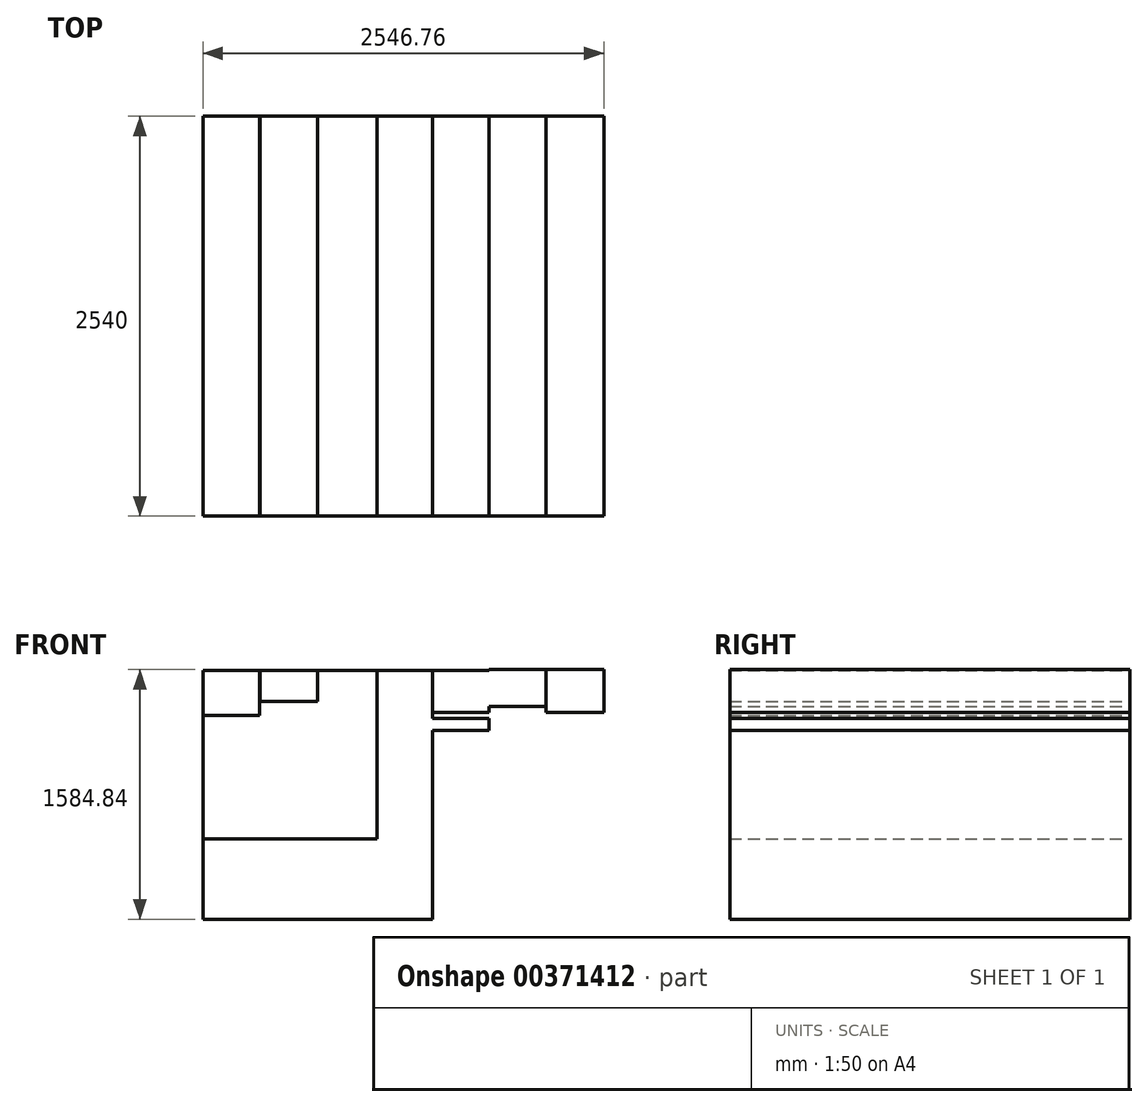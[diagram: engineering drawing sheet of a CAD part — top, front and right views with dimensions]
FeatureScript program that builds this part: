
annotation { "Feature Type Name" : "Feature", "Feature Type Description" : "" }
export const myFeature = defineFeature(function(context is Context, id is Id, definition is map)
    precondition{}
    {
        {
            var Q0;
            Q0=qCreatedBy(makeId("Front.planeOp"),FACE);
            var sketch = newSketch(context, id + "F0", { "sketchPlane" : qUnion([Q0])});
            skLineSegment(sketch, "E0", {"start": v(-1277.32, 1268.25) * mm, "end": v(-1277.32, -1271.75) * mm});
            skLineSegment(sketch, "E1", {"start": v(-1277.32, -1271.75) * mm, "end": v(1269.44, -1271.75) * mm});
            skLineSegment(sketch, "E2", {"start": v(1269.44, -1271.75) * mm, "end": v(1269.44, 1273.33) * mm});
            skLineSegment(sketch, "E3", {"start": v(1269.44, 1273.33) * mm, "end": v(-1277.32, 1268.25) * mm});
            skLineSegment(sketch, "E4", {"start": v(-1277.32, 1268.25) * mm, "end": v(-914.1, 1268.98) * mm});
            skLineSegment(sketch, "E5", {"start": v(-914.1, 1268.98) * mm, "end": v(-550.88, 1269.7) * mm});
            skLineSegment(sketch, "E6", {"start": v(-550.88, 1269.7) * mm, "end": v(-187.66, 1270.42) * mm});
            skLineSegment(sketch, "E7", {"start": v(-187.66, 1270.42) * mm, "end": v(175.56, 1271.15) * mm});
            skLineSegment(sketch, "E8", {"start": v(175.56, 1271.15) * mm, "end": v(538.78, 1271.87) * mm});
            skLineSegment(sketch, "E9", {"start": v(538.78, 1271.87) * mm, "end": v(902, 1272.6) * mm});
            skLineSegment(sketch, "E10", {"start": v(902, 1272.6) * mm, "end": v(1269.44, 1273.33) * mm});
            skLineSegment(sketch, "E11.bottom", {"start": v(-1277.32, 1268.25) * mm, "end": v(-917.92, 1268.25) * mm});
            skLineSegment(sketch, "E11.top", {"start": v(-1277.32, 980.21) * mm, "end": v(-917.92, 980.21) * mm});
            skLineSegment(sketch, "E11.left", {"start": v(-1277.32, 1268.25) * mm, "end": v(-1277.32, 980.21) * mm});
            skLineSegment(sketch, "E11.right", {"start": v(-917.92, 1268.25) * mm, "end": v(-917.92, 980.21) * mm});
            skLineSegment(sketch, "E12.bottom", {"start": v(-914.1, 1268.98) * mm, "end": v(-550.13, 1268.98) * mm});
            skLineSegment(sketch, "E12.top", {"start": v(-914.1, 1071.1) * mm, "end": v(-550.13, 1071.1) * mm});
            skLineSegment(sketch, "E12.left", {"start": v(-914.1, 1268.98) * mm, "end": v(-914.1, 1071.1) * mm});
            skLineSegment(sketch, "E12.right", {"start": v(-550.13, 1268.98) * mm, "end": v(-550.13, 1071.1) * mm});
            skLineSegment(sketch, "E13.bottom", {"start": v(-1277.32, 1268.25) * mm, "end": v(-172.42, 1268.25) * mm});
            skLineSegment(sketch, "E13.top", {"start": v(-1277.32, 195.83) * mm, "end": v(-172.42, 195.83) * mm});
            skLineSegment(sketch, "E13.left", {"start": v(-1277.32, 1268.25) * mm, "end": v(-1277.32, 195.83) * mm});
            skLineSegment(sketch, "E13.right", {"start": v(-172.42, 1268.25) * mm, "end": v(-172.42, 195.83) * mm});
            skLineSegment(sketch, "E14.bottom", {"start": v(-1277.32, 1268.25) * mm, "end": v(180.77, 1268.25) * mm});
            skLineSegment(sketch, "E14.top", {"start": v(-1277.32, -312.97) * mm, "end": v(180.77, -312.97) * mm});
            skLineSegment(sketch, "E14.left", {"start": v(-1277.32, 1268.25) * mm, "end": v(-1277.32, -312.97) * mm});
            skLineSegment(sketch, "E14.right", {"start": v(180.77, 1268.25) * mm, "end": v(180.77, -312.97) * mm});
            skLineSegment(sketch, "E15.bottom", {"start": v(180.77, 1268.25) * mm, "end": v(538.78, 1268.25) * mm});
            skLineSegment(sketch, "E15.top", {"start": v(180.77, 1000.53) * mm, "end": v(538.78, 1000.53) * mm});
            skLineSegment(sketch, "E15.left", {"start": v(180.77, 1268.25) * mm, "end": v(180.77, 1000.53) * mm});
            skLineSegment(sketch, "E15.right", {"start": v(538.78, 1268.25) * mm, "end": v(538.78, 1000.53) * mm});
            skLineSegment(sketch, "E16.bottom", {"start": v(538.78, 1271.87) * mm, "end": v(902, 1271.87) * mm});
            skLineSegment(sketch, "E16.top", {"start": v(538.78, 1038.28) * mm, "end": v(902, 1038.28) * mm});
            skLineSegment(sketch, "E16.left", {"start": v(538.78, 1271.87) * mm, "end": v(538.78, 1038.28) * mm});
            skLineSegment(sketch, "E16.right", {"start": v(902, 1271.87) * mm, "end": v(902, 1038.28) * mm});
            skLineSegment(sketch, "E17.bottom", {"start": v(902, 1271.87) * mm, "end": v(1269.44, 1271.87) * mm});
            skLineSegment(sketch, "E17.top", {"start": v(902, 1000.53) * mm, "end": v(1269.44, 1000.53) * mm});
            skLineSegment(sketch, "E17.left", {"start": v(902, 1271.87) * mm, "end": v(902, 1000.53) * mm});
            skLineSegment(sketch, "E17.right", {"start": v(1269.44, 1271.87) * mm, "end": v(1269.44, 1000.53) * mm});
            skLineSegment(sketch, "E18", {"start": v(-1277.32, 1268.25) * mm, "end": v(-1277.32, 963.45) * mm});
            skLineSegment(sketch, "E19", {"start": v(-1277.32, 963.45) * mm, "end": v(-1277.32, 1268.25) * mm});
            skLineSegment(sketch, "E20", {"start": v(-1277.32, 887.25) * mm, "end": v(-1277.32, 1268.25) * mm});
            skLineSegment(sketch, "E21.bottom", {"start": v(538.78, 963.45) * mm, "end": v(180.77, 963.45) * mm});
            skLineSegment(sketch, "E21.top", {"start": v(538.78, 887.25) * mm, "end": v(180.77, 887.25) * mm});
            skLineSegment(sketch, "E21.left", {"start": v(538.78, 963.45) * mm, "end": v(538.78, 887.25) * mm});
            skLineSegment(sketch, "E21.right", {"start": v(180.77, 963.45) * mm, "end": v(180.77, 887.25) * mm});
            skSolve(sketch);
        }
        {
            var Q0;
            {var subQ0=sQuery(id+"F0.wireOp",EDGE,"E11.top");Q0=makeQuery(id+"F0.imprint","IMPRINT",FACE,{"disambiguationData":[TD([[makeQuery(id+"F0.imprint","IMPRINT",EDGE,{"derivedFrom":subQ0}),1.0]])]});}
            var Q1;
            {var subQ3=sQuery(id+"F0.wireOp",EDGE,"E16.bottom");Q1=makeQuery(id+"F0.imprint","IMPRINT",FACE,{"disambiguationData":[TD([[makeQuery(id+"F0.imprint","IMPRINT",EDGE,{"derivedFrom":subQ3}),-1.0]])]});}
            extrude(context, id + "F1", {"entities" : qUnion([Q0, Q1]), "depth" : 2540 * mm});
        }
        {
            var Q0;
            {var subQ0=sQuery(id+"F0.wireOp",EDGE,"E12.top");Q0=makeQuery(id+"F0.imprint","IMPRINT",FACE,{"disambiguationData":[TD([[makeQuery(id+"F0.imprint","IMPRINT",EDGE,{"derivedFrom":subQ0}),1.0]])]});}
            var Q1;
            {var subQ1=sQuery(id+"F0.wireOp",EDGE,"E15.bottom");Q1=makeQuery(id+"F0.imprint","IMPRINT",FACE,{"disambiguationData":[TD([[makeQuery(id+"F0.imprint","IMPRINT",EDGE,{"derivedFrom":subQ1}),-1.0]])]});}
            extrude(context, id + "F2", {"entities" : qUnion([Q0, Q1]), "operationType" : NewBodyOperationType.ADD, "depth" : 2540 * mm});
        }
        {
            var Q0;
            {var subQ9=sQuery(id+"F0.wireOp",EDGE,"E11.top");Q0=makeQuery(id+"F0.imprint","IMPRINT",FACE,{"disambiguationData":[TD([[makeQuery(id+"F0.imprint","IMPRINT",EDGE,{"derivedFrom":subQ9}),-1.0]])]});}
            var Q1;
            {var subQ4=sQuery(id+"F0.wireOp",EDGE,"E13.top");Q1=makeQuery(id+"F0.imprint","IMPRINT",FACE,{"disambiguationData":[TD([[makeQuery(id+"F0.imprint","IMPRINT",EDGE,{"derivedFrom":subQ4}),-1.0]])]});}
            var Q2;
            Q2=makeQuery(id+"F0.imprint","IMPRINT",FACE,{"disambiguationData":[TD([[makeQuery(id+"F0.imprint","IMPRINT",EDGE,{"derivedFrom":sQuery(id+"F0.wireOp",EDGE,"E21.bottom")}),1.0]])]});
            extrude(context, id + "F3", {"entities" : qUnion([Q0, Q1, Q2]), "depth" : 2540 * mm});
        }
        {
            var Q0;
            {var subQ3=sQuery(id+"F0.wireOp",EDGE,"E17.bottom");Q0=makeQuery(id+"F0.imprint","IMPRINT",FACE,{"disambiguationData":[TD([[makeQuery(id+"F0.imprint","IMPRINT",EDGE,{"derivedFrom":subQ3}),-1.0]])]});}
            var Q1;
            Q1=makeQuery(id+"F0.imprint","IMPRINT",FACE,{"disambiguationData":[TD([[makeQuery(id+"F0.imprint","IMPRINT",EDGE,{"derivedFrom":sQuery(id+"F0.wireOp",EDGE,"E0")}),1.0]])]});
            extrude(context, id + "F4", {"entities" : qUnion([Q0, Q1]), "depth" : 2540 * mm});
        }
    });
